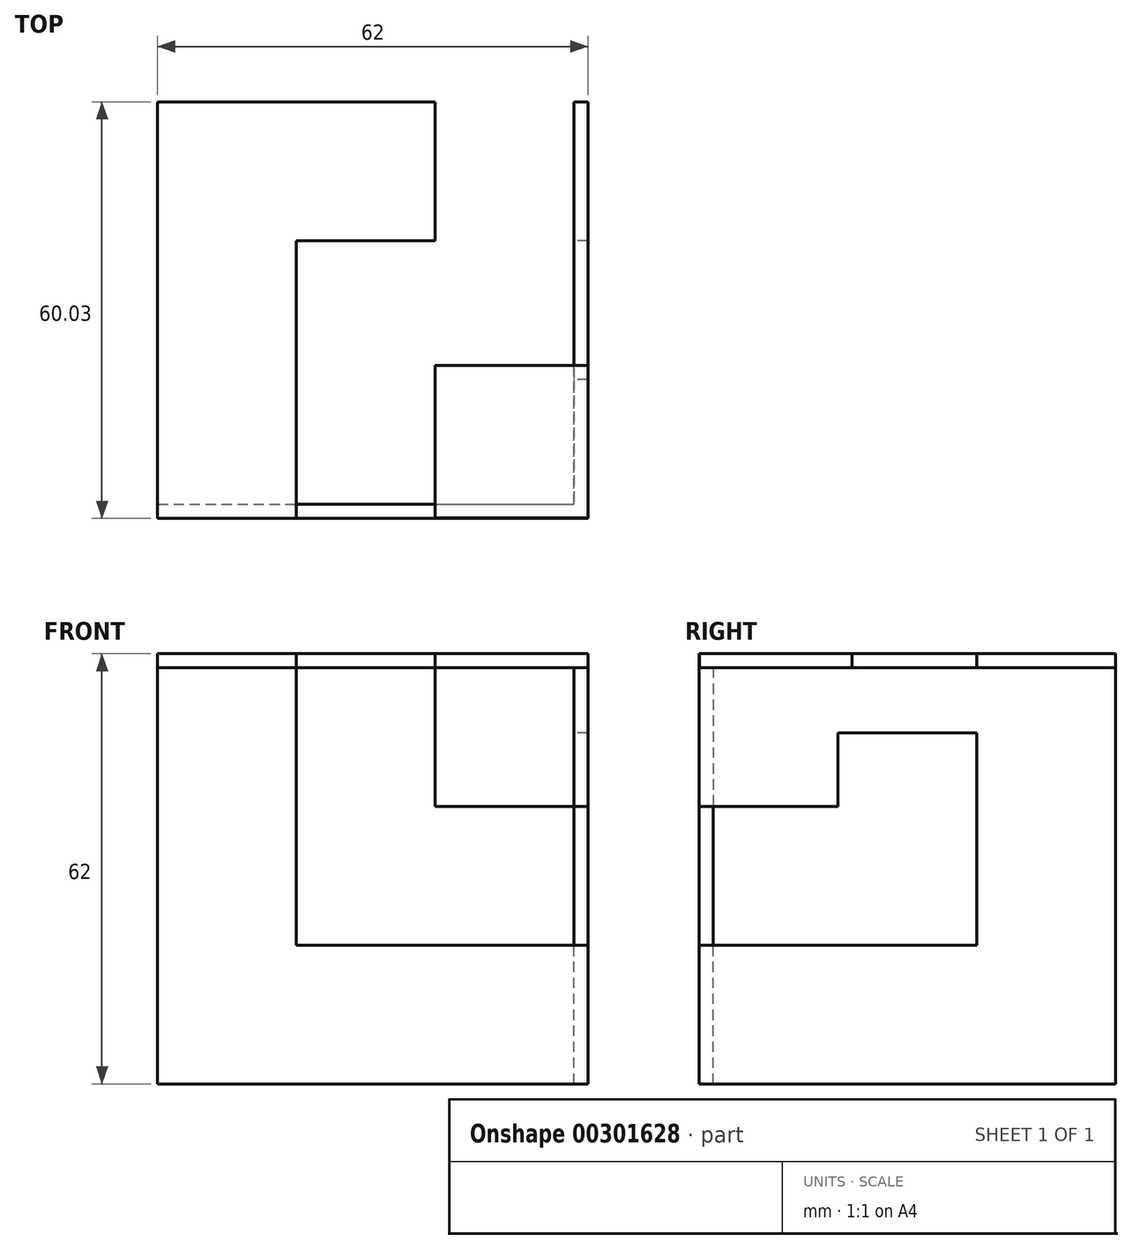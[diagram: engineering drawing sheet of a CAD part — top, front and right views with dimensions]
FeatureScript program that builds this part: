
annotation { "Feature Type Name" : "Feature", "Feature Type Description" : "" }
export const myFeature = defineFeature(function(context is Context, id is Id, definition is map)
    precondition{}
    {
        {
            var Q0;
            Q0=qCreatedBy(makeId("Front.planeOp"),FACE);
            var sketch = newSketch(context, id + "F0", { "sketchPlane" : qUnion([Q0])});
            skLineSegment(sketch, "E0.bottom", {"start": v(-45.89, 27.82) * mm, "end": v(-25.89, 27.82) * mm});
            skLineSegment(sketch, "E0.top", {"start": v(-45.89, -32.18) * mm, "end": v(-25.89, -32.18) * mm});
            skLineSegment(sketch, "E0.left", {"start": v(-45.89, 27.82) * mm, "end": v(-45.89, -32.18) * mm});
            skLineSegment(sketch, "E0.right", {"start": v(-25.89, 27.82) * mm, "end": v(-25.89, -32.18) * mm});
            skLineSegment(sketch, "E1.bottom", {"start": v(-45.89, -32.18) * mm, "end": v(14.11, -32.18) * mm});
            skLineSegment(sketch, "E1.top", {"start": v(-45.89, -12.18) * mm, "end": v(14.11, -12.18) * mm});
            skLineSegment(sketch, "E1.left", {"start": v(-45.89, -32.18) * mm, "end": v(-45.89, -12.18) * mm});
            skLineSegment(sketch, "E1.right", {"start": v(14.11, -32.18) * mm, "end": v(14.11, -12.18) * mm});
            skLineSegment(sketch, "E2.bottom", {"start": v(-5.89, 27.82) * mm, "end": v(14.11, 27.82) * mm});
            skLineSegment(sketch, "E2.top", {"start": v(-5.89, 7.82) * mm, "end": v(14.11, 7.82) * mm});
            skLineSegment(sketch, "E2.left", {"start": v(-5.89, 27.82) * mm, "end": v(-5.89, 7.82) * mm});
            skLineSegment(sketch, "E2.right", {"start": v(14.11, 27.82) * mm, "end": v(14.11, 7.82) * mm});
            skSolve(sketch);
        }
        {
            var Q0;
            Q0 = qSketchRegion(id + "F0", true);
            extrude(context, id + "F1", {"entities" : qUnion([Q0]), "depth" : 2 * mm});
        }
        {
            var Q0;
            Q0=makeQuery(id+"F1.opExtrude","SWEPT_FACE",FACE,{"disambiguationData":[OSD([sQuery(id+"F0.wireOp",EDGE,"E1.right")])]});
            var sketch = newSketch(context, id + "F2", { "sketchPlane" : qUnion([Q0])});
            skLineSegment(sketch, "E3.bottom", {"start": v(-2, -32.18) * mm, "end": v(58, -32.18) * mm});
            skLineSegment(sketch, "E3.top", {"start": v(-2, -12.18) * mm, "end": v(58, -12.18) * mm});
            skLineSegment(sketch, "E3.left", {"start": v(-2, -32.18) * mm, "end": v(-2, -12.18) * mm});
            skLineSegment(sketch, "E3.right", {"start": v(58, -32.18) * mm, "end": v(58, -12.18) * mm});
            skLineSegment(sketch, "E4.bottom", {"start": v(58, -32.18) * mm, "end": v(38, -32.18) * mm});
            skLineSegment(sketch, "E4.top", {"start": v(58, 27.82) * mm, "end": v(38, 27.82) * mm});
            skLineSegment(sketch, "E4.left", {"start": v(58, -32.18) * mm, "end": v(58, 27.82) * mm});
            skLineSegment(sketch, "E4.right", {"start": v(38, -32.18) * mm, "end": v(38, 27.82) * mm});
            skLineSegment(sketch, "E5.left", {"start": v(38, 27.82) * mm, "end": v(38, 18.38) * mm});
            skLineSegment(sketch, "E6.bottom", {"start": v(17.97, 27.82) * mm, "end": v(-2.03, 27.82) * mm});
            skLineSegment(sketch, "E6.top", {"start": v(17.97, 7.82) * mm, "end": v(-2.03, 7.82) * mm});
            skLineSegment(sketch, "E6.left", {"start": v(17.97, 27.82) * mm, "end": v(17.97, 7.82) * mm});
            skLineSegment(sketch, "E6.right", {"start": v(-2.03, 27.82) * mm, "end": v(-2.03, 7.82) * mm});
            skLineSegment(sketch, "E7", {"start": v(38, 27.82) * mm, "end": v(17.97, 27.82) * mm});
            skLineSegment(sketch, "E8", {"start": v(38, 18.38) * mm, "end": v(17.97, 18.38) * mm});
            skSolve(sketch);
        }
        {
            var Q0;
            Q0 = qSketchRegion(id + "F2", true);
            extrude(context, id + "F3", {"entities" : qUnion([Q0]), "operationType" : NewBodyOperationType.ADD, "depth" : 2 * mm});
        }
        {
            var Q0;
            Q0=makeQuery(id+"F1.opExtrude","SWEPT_FACE",FACE,{"disambiguationData":[OSD([sQuery(id+"F0.wireOp",EDGE,"E0.bottom")])]});
            var sketch = newSketch(context, id + "F4", { "sketchPlane" : qUnion([Q0])});
            skLineSegment(sketch, "E9.bottom", {"start": v(-45.89, -2) * mm, "end": v(-25.89, -2) * mm});
            skLineSegment(sketch, "E9.top", {"start": v(-45.89, 58) * mm, "end": v(-25.89, 58) * mm});
            skLineSegment(sketch, "E9.left", {"start": v(-45.89, -2) * mm, "end": v(-45.89, 58) * mm});
            skLineSegment(sketch, "E9.right", {"start": v(-25.89, -2) * mm, "end": v(-25.89, 58) * mm});
            skLineSegment(sketch, "E10.bottom", {"start": v(-45.89, 58) * mm, "end": v(-5.89, 58) * mm});
            skLineSegment(sketch, "E10.top", {"start": v(-45.89, 38) * mm, "end": v(-5.89, 38) * mm});
            skLineSegment(sketch, "E10.left", {"start": v(-45.89, 58) * mm, "end": v(-45.89, 38) * mm});
            skLineSegment(sketch, "E10.right", {"start": v(-5.89, 58) * mm, "end": v(-5.89, 38) * mm});
            skLineSegment(sketch, "E11.bottom", {"start": v(16.11, -1.96) * mm, "end": v(-5.89, -1.96) * mm});
            skLineSegment(sketch, "E11.top", {"start": v(16.11, 20.04) * mm, "end": v(-5.89, 20.04) * mm});
            skLineSegment(sketch, "E11.left", {"start": v(16.11, -1.96) * mm, "end": v(16.11, 20.04) * mm});
            skLineSegment(sketch, "E11.right", {"start": v(-5.89, -1.96) * mm, "end": v(-5.89, 20.04) * mm});
            skSolve(sketch);
        }
        {
            var Q0;
            Q0 = qSketchRegion(id + "F4", true);
            extrude(context, id + "F5", {"entities" : qUnion([Q0]), "depth" : 2 * mm});
        }
    });
